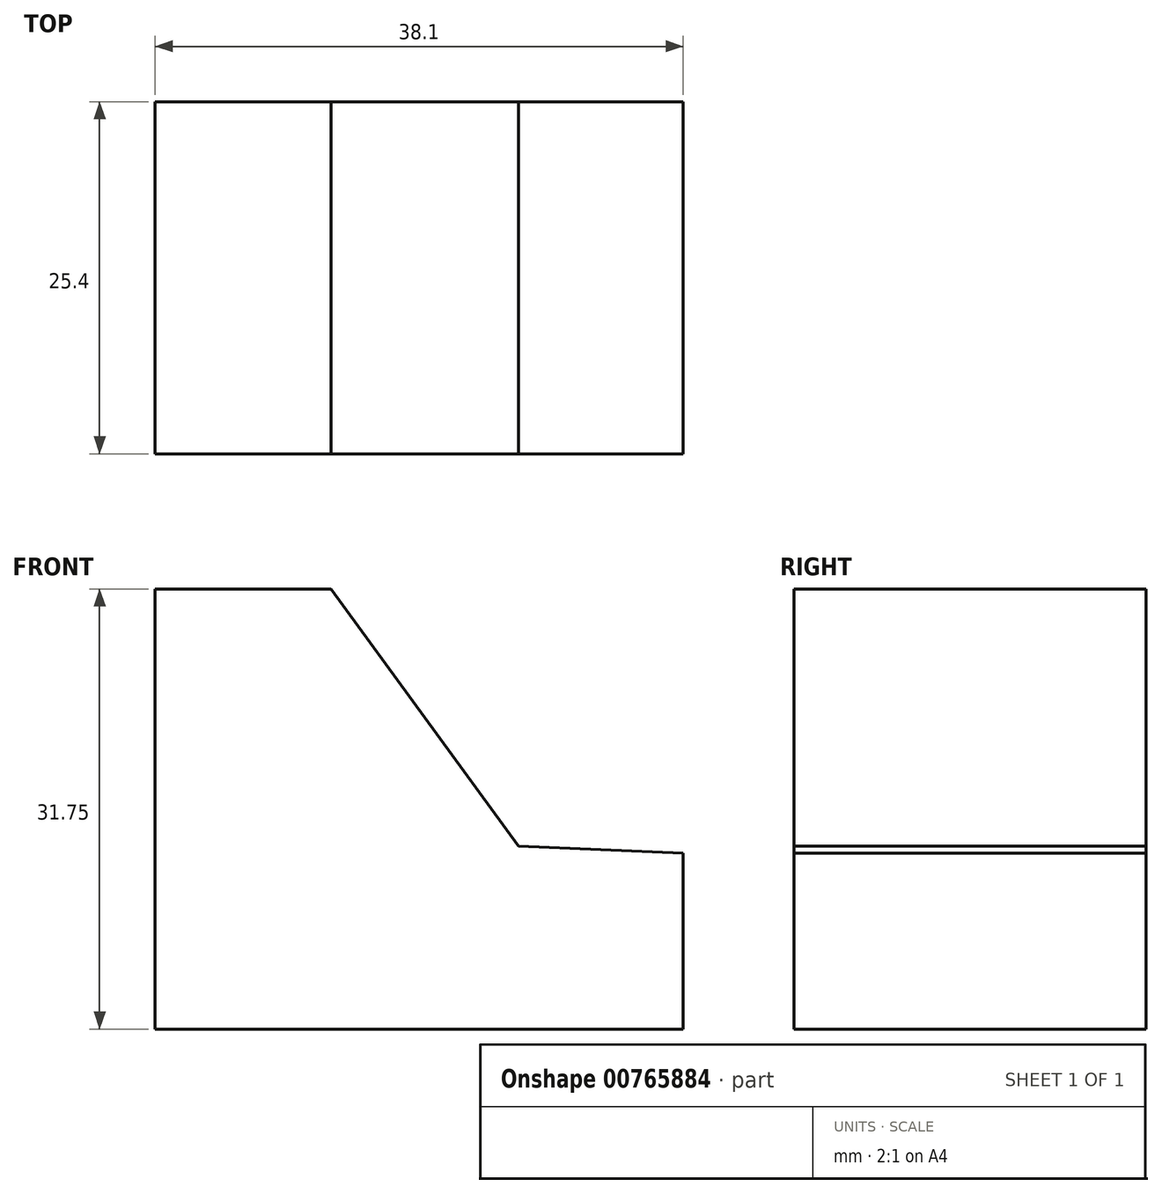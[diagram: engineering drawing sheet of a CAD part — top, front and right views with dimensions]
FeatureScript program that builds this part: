
annotation { "Feature Type Name" : "Feature", "Feature Type Description" : "" }
export const myFeature = defineFeature(function(context is Context, id is Id, definition is map)
    precondition{}
    {
        {
            var Q0;
            Q0=qCreatedBy(makeId("Front.planeOp"),FACE);
            var sketch = newSketch(context, id + "F0", { "sketchPlane" : qUnion([Q0])});
            skLineSegment(sketch, "E0", {"start": v(0, 0) * mm, "end": v(38.1, 0) * mm});
            skLineSegment(sketch, "E1", {"start": v(38.1, 0) * mm, "end": v(38.1, 12.7) * mm});
            skLineSegment(sketch, "E2", {"start": v(0, 0) * mm, "end": v(0, 31.75) * mm});
            skLineSegment(sketch, "E3", {"start": v(0, 31.75) * mm, "end": v(12.7, 31.75) * mm});
            skLineSegment(sketch, "E4", {"start": v(12.7, 31.75) * mm, "end": v(26.2, 13.18) * mm});
            skLineSegment(sketch, "E5", {"start": v(38.1, 12.7) * mm, "end": v(26.2, 13.18) * mm});
            skSolve(sketch);
        }
        {
            var Q0;
            Q0 = qSketchRegion(id + "F0", true);
            extrude(context, id + "F1", {"entities" : qUnion([Q0]), "depth" : 25.4 * mm, "offsetDistance" : 25.4 * mm});
        }
    });
